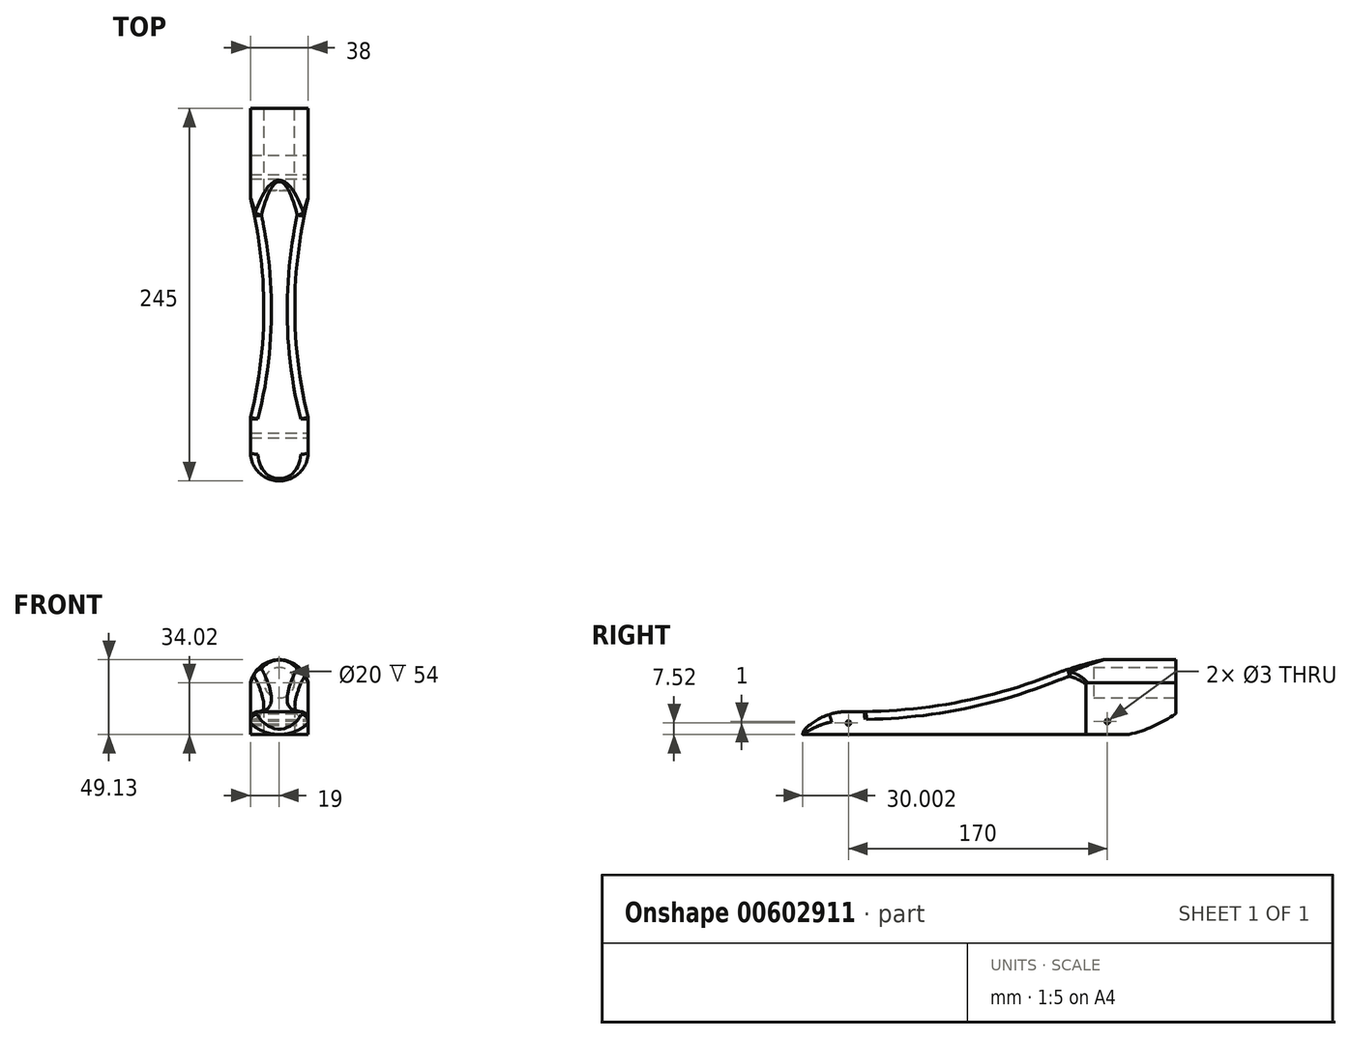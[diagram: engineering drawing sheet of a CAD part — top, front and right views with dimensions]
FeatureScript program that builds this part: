
annotation { "Feature Type Name" : "Feature", "Feature Type Description" : "" }
export const myFeature = defineFeature(function(context is Context, id is Id, definition is map)
    precondition{}
    {
        {
            var Q0;
            Q0=qCreatedBy(makeId("Right.planeOp"),FACE);
            var sketch = newSketch(context, id + "F0", { "sketchPlane" : qUnion([Q0])});
            skLineSegment(sketch, "E0", {"start": v(-162.96, -20) * mm, "end": v(137.04, -20) * mm});
            skLineSegment(sketch, "E1", {"start": v(137.04, -20) * mm, "end": v(137.04, 50) * mm});
            skLineSegment(sketch, "E2", {"start": v(137.04, 50) * mm, "end": v(-162.96, 0) * mm});
            skLineSegment(sketch, "E3", {"start": v(-162.96, 0) * mm, "end": v(-162.96, -20) * mm});
            skSolve(sketch);
        }
        {
            var Q0;
            Q0=makeQuery(id+"F0.imprint","IMPRINT",FACE,{"disambiguationData":[TD([[makeQuery(id+"F0.imprint","IMPRINT",EDGE,{"derivedFrom":sQuery(id+"F0.wireOp",EDGE,"E0")}),1.0]])]});
            extrude(context, id + "F1", {"entities" : qUnion([Q0]), "depth" : 42 * mm, "offsetDistance" : 25 * mm});
        }
        {
            var Q0;
            Q0=makeQuery(id+"F1.opExtrude","SWEPT_FACE",FACE,{"disambiguationData":[OSD([sQuery(id+"F0.wireOp",EDGE,"E1")])]});
            var sketch = newSketch(context, id + "F2", { "sketchPlane" : qUnion([Q0])});
            skCircle(sketch, "E4", {"center": v(-21, 14) * mm, "radius": 10 * mm});
            skSolve(sketch);
        }
        {
            var Q0;
            Q0=makeQuery(id+"F2.imprint","IMPRINT",FACE,{"disambiguationData":[TD([[makeQuery(id+"F2.imprint","IMPRINT",EDGE,{"derivedFrom":sQuery(id+"F2.wireOp",EDGE,"E4")}),1.0]])]});
            extrude(context, id + "F3", {"entities" : qUnion([Q0]), "operationType" : NewBodyOperationType.REMOVE, "oppositeDirection" : true, "depth" : 54 * mm, "offsetDistance" : 25 * mm});
        }
        {
            var Q0;
            Q0=makeQuery(id+"F1.opExtrude","CAP_FACE",FACE,{"disambiguationData":[OSD([sQuery(id+"F0.wireOp",EDGE,"E0"),sQuery(id+"F0.wireOp",EDGE,"E1"),sQuery(id+"F0.wireOp",EDGE,"E2"),sQuery(id+"F0.wireOp",EDGE,"E3")])],"isStart":false});
            var sketch = newSketch(context, id + "F4", { "sketchPlane" : qUnion([Q0])});
            skLineSegment(sketch, "E5", {"start": v(-107.96, -20) * mm, "end": v(-107.96, -18) * mm});
            skArc(sketch, "E6", {"start": v(-77.8, -5) * mm, "mid": v(-10.9, 0.35) * mm, "end": v(53.75, 18.37) * mm});
            skArc(sketch, "E7", {"start": v(137.04, 35) * mm, "mid": v(94.68, 30.25) * mm, "end": v(53.75, 18.37) * mm});
            skArc(sketch, "E8", {"start": v(-77.8, -5) * mm, "mid": v(-94.27, -8.26) * mm, "end": v(-107.96, -18) * mm});
            skArc(sketch, "E9", {"start": v(106.2, -20) * mm, "mid": v(122.27, -14.6) * mm, "end": v(137.04, -6.3) * mm});
            skCircle(sketch, "E10", {"center": v(92.04, -11.5) * mm, "radius": 1.5 * mm});
            skCircle(sketch, "E11", {"center": v(-77.96, -12.5) * mm, "radius": 1.5 * mm});
            skLineSegment(sketch, "E12", {"start": v(-107.96, -20) * mm, "end": v(106.2, -20) * mm});
            skSolve(sketch);
        }
        {
            var Q0;
            {var subQ3=sQuery(id+"F4.wireOp",EDGE,"E5");Q0=makeQuery(id+"F4.imprint","IMPRINT",FACE,{"disambiguationData":[TD([[makeQuery(id+"F4.imprint","IMPRINT",EDGE,{"derivedFrom":subQ3}),1.0]])]});}
            var Q1;
            Q1=makeQuery(id+"F4.imprint","IMPRINT",FACE,{"disambiguationData":[TD([[makeQuery(id+"F4.imprint","IMPRINT",EDGE,{"derivedFrom":sQuery(id+"F4.wireOp",EDGE,"E11")}),1.0]])]});
            var Q2;
            {var subQ0=sQuery(id+"F4.wireOp",EDGE,"E9");Q2=makeQuery(id+"F4.imprint","IMPRINT",FACE,{"disambiguationData":[TD([[makeQuery(id+"F4.imprint","IMPRINT",EDGE,{"derivedFrom":subQ0}),-1.0]])]});}
            var Q3;
            Q3=makeQuery(id+"F4.imprint","IMPRINT",FACE,{"disambiguationData":[TD([[makeQuery(id+"F4.imprint","IMPRINT",EDGE,{"derivedFrom":sQuery(id+"F4.wireOp",EDGE,"E10")}),1.0]])]});
            extrude(context, id + "F5", {"entities" : qUnion([Q0, Q1, Q2, Q3]), "operationType" : NewBodyOperationType.REMOVE, "oppositeDirection" : true, "depth" : 100 * mm, "offsetDistance" : 25 * mm});
        }
        {
            var Q0;
            Q0=makeQuery(id+"F1.opExtrude","SWEPT_FACE",FACE,{"disambiguationData":[OSD([sQuery(id+"F0.wireOp",EDGE,"E0")])]});
            var sketch = newSketch(context, id + "F6", { "sketchPlane" : qUnion([Q0])});
            skLineSegment(sketch, "E13.bottom", {"start": v(2, 111.66) * mm, "end": v(-16.59, 111.66) * mm});
            skLineSegment(sketch, "E13.top", {"start": v(2, -139.51) * mm, "end": v(-16.59, -139.51) * mm});
            skLineSegment(sketch, "E13.left", {"start": v(2, 111.66) * mm, "end": v(2, -139.51) * mm});
            skLineSegment(sketch, "E13.right", {"start": v(-16.59, 111.66) * mm, "end": v(-16.59, -139.51) * mm});
            skPoint(sketch, "E14.firstSnap0", {"position": v(-7.3, 111.66) * mm});
            skLineSegment(sketch, "E14.bottom", {"start": v(40, 111.66) * mm, "end": v(60.24, 111.66) * mm});
            skLineSegment(sketch, "E14.top", {"start": v(40, -140.75) * mm, "end": v(60.24, -140.75) * mm});
            skLineSegment(sketch, "E14.left", {"start": v(40, 111.66) * mm, "end": v(40, -140.75) * mm});
            skLineSegment(sketch, "E14.right", {"start": v(60.24, 111.66) * mm, "end": v(60.24, -140.75) * mm});
            skLineSegment(sketch, "E15", {"start": v(2, 88.96) * mm, "end": v(40, 88.96) * mm});
            skArc(sketch, "E16", {"start": v(40, 88.96) * mm, "mid": v(21, 107.96) * mm, "end": v(2, 88.96) * mm});
            skSolve(sketch);
        }
        {
            var Q0;
            {var subQ0=sQuery(id+"F0.wireOp",EDGE,"E0");var subQ1=makeQuery(id+"F1.opExtrude","CAP_EDGE",EDGE,{"disambiguationData":[OSD([subQ0])],"isStart":true});Q0=makeQuery(id+"F6.imprint","IMPRINT",FACE,{"disambiguationData":[TD([[makeQuery(id+"F6.imprint","IMPRINT",EDGE,{"derivedFrom":subQ1}),1.0]])]});}
            var Q1;
            {var subQ0=sQuery(id+"F0.wireOp",EDGE,"E0");var subQ1=makeQuery(id+"F1.opExtrude","CAP_EDGE",EDGE,{"disambiguationData":[OSD([subQ0])],"isStart":false});Q1=makeQuery(id+"F6.imprint","IMPRINT",FACE,{"disambiguationData":[TD([[makeQuery(id+"F6.imprint","IMPRINT",EDGE,{"derivedFrom":subQ1}),-1.0]])]});}
            var Q2;
            {var subQ1=sQuery(id+"F6.wireOp",EDGE,"E14.bottom");Q2=makeQuery(id+"F6.imprint","IMPRINT",FACE,{"disambiguationData":[TD([[makeQuery(id+"F6.imprint","IMPRINT",EDGE,{"derivedFrom":subQ1}),-1.0]])]});}
            var Q3;
            {var subQ1=sQuery(id+"F6.wireOp",EDGE,"E13.bottom");Q3=makeQuery(id+"F6.imprint","IMPRINT",FACE,{"disambiguationData":[TD([[makeQuery(id+"F6.imprint","IMPRINT",EDGE,{"derivedFrom":subQ1}),1.0]])]});}
            var Q4;
            {var subQ0=sQuery(id+"F6.wireOp",EDGE,"E16");var subQ1=sQuery(id+"F6.wireOp",EDGE,"E13.left");var subQ2=makeQuery(id+"F6.imprint","INTERSECT",VERTEX,{"derivedFrom":[subQ1,sQuery(id+"F6.wireOp",EDGE,"E15"),subQ0]});Q4=makeQuery(id+"F6.imprint","IMPRINT",FACE,{"disambiguationData":[TD([[makeQuery(id+"F6.imprint","IMPRINT",EDGE,{"disambiguationData":[TD([[subQ2,1.0]])],"derivedFrom":subQ1}),1.0]])]});}
            var Q5;
            {var subQ0=sQuery(id+"F6.wireOp",EDGE,"E16");var subQ1=sQuery(id+"F6.wireOp",EDGE,"E14.left");var subQ2=makeQuery(id+"F6.imprint","INTERSECT",VERTEX,{"derivedFrom":[subQ1,sQuery(id+"F6.wireOp",EDGE,"E15"),subQ0]});Q5=makeQuery(id+"F6.imprint","IMPRINT",FACE,{"disambiguationData":[TD([[makeQuery(id+"F6.imprint","IMPRINT",EDGE,{"disambiguationData":[TD([[subQ2,1.0]])],"derivedFrom":subQ1}),-1.0]])]});}
            extrude(context, id + "F7", {"entities" : qUnion([Q0, Q1, Q2, Q3, Q4, Q5]), "operationType" : NewBodyOperationType.REMOVE, "oppositeDirection" : true, "depth" : 100 * mm, "offsetDistance" : 25 * mm});
        }
        {
            var Q0;
            Q0=makeQuery(id+"F1.opExtrude","SWEPT_FACE",FACE,{"disambiguationData":[OSD([sQuery(id+"F0.wireOp",EDGE,"E1")])]});
            var sketch = newSketch(context, id + "F8", { "sketchPlane" : qUnion([Q0])});
            skLineSegment(sketch, "E17", {"start": v(-40, 14) * mm, "end": v(-2, 14) * mm});
            skArc(sketch, "E18", {"start": v(-2, 14) * mm, "mid": v(-21, 29.11) * mm, "end": v(-40, 14) * mm});
            skSolve(sketch);
        }
        {
            var Q0;
            {var subQ0=sQuery(id+"F8.wireOp",EDGE,"E18");Q0=makeQuery(id+"F8.imprint","IMPRINT",FACE,{"disambiguationData":[TD([[makeQuery(id+"F8.imprint","IMPRINT",EDGE,{"derivedFrom":subQ0}),-1.0]])]});}
            extrude(context, id + "F9", {"entities" : qUnion([Q0]), "operationType" : NewBodyOperationType.REMOVE, "oppositeDirection" : true, "depth" : 300 * mm, "offsetDistance" : 25 * mm});
        }
        {
            var Q0;
            Q0=makeQuery(id+"F1.opExtrude","SWEPT_FACE",FACE,{"disambiguationData":[OSD([sQuery(id+"F0.wireOp",EDGE,"E0")])]});
            var sketch = newSketch(context, id + "F10", { "sketchPlane" : qUnion([Q0])});
            skArc(sketch, "E19", {"start": v(40, 66.64) * mm, "mid": v(31.16, -5.63) * mm, "end": v(40, -77.9) * mm});
            skArc(sketch, "E20", {"start": v(2, -77.9) * mm, "mid": v(10.84, -5.63) * mm, "end": v(2, 66.64) * mm});
            skLineSegment(sketch, "E21", {"start": v(40, 66.64) * mm, "end": v(40, -77.9) * mm});
            skLineSegment(sketch, "E22", {"start": v(2, 66.64) * mm, "end": v(2, -77.9) * mm});
            skSolve(sketch);
        }
        {
            var Q0;
            Q0=makeQuery(id+"F10.imprint","IMPRINT",FACE,{"disambiguationData":[TD([[makeQuery(id+"F10.imprint","IMPRINT",EDGE,{"derivedFrom":sQuery(id+"F10.wireOp",EDGE,"E20")}),1.0]])]});
            var Q1;
            Q1=makeQuery(id+"F10.imprint","IMPRINT",FACE,{"disambiguationData":[TD([[makeQuery(id+"F10.imprint","IMPRINT",EDGE,{"derivedFrom":sQuery(id+"F10.wireOp",EDGE,"E19")}),1.0]])]});
            extrude(context, id + "F11", {"entities" : qUnion([Q0, Q1]), "operationType" : NewBodyOperationType.REMOVE, "oppositeDirection" : true, "depth" : 100 * mm, "offsetDistance" : 25 * mm});
        }
        {
            var Q0;
            Q0=makeQuery(id+"F9.boolean.opBoolean","INTERSECT",EDGE,{"derivedFrom":[makeQuery(id+"F5.boolean.opBoolean","COPY",FACE,{"derivedFrom":makeQuery(id+"F5.opExtrude","SWEPT_FACE",FACE,{"disambiguationData":[OSD([sQuery(id+"F4.wireOp",EDGE,"E7")])]})}),makeQuery(id+"F9.opExtrude","SWEPT_FACE",FACE,{"disambiguationData":[OSD([sQuery(id+"F8.wireOp",EDGE,"E18")])]})]});
            var Q1;
            Q1=makeQuery(id+"F11.boolean.opBoolean","INTERSECT",EDGE,{"derivedFrom":[makeQuery(id+"F5.boolean.opBoolean","COPY",FACE,{"derivedFrom":makeQuery(id+"F5.opExtrude","SWEPT_FACE",FACE,{"disambiguationData":[OSD([sQuery(id+"F4.wireOp",EDGE,"E6")])]})}),makeQuery(id+"F11.opExtrude","SWEPT_FACE",FACE,{"disambiguationData":[OSD([sQuery(id+"F10.wireOp",EDGE,"E19")])]})]});
            var Q2;
            Q2=makeQuery(id+"F5.boolean.opBoolean","COPY",EDGE,{"derivedFrom":makeQuery(id+"F5.opExtrude","SWEPT_EDGE",EDGE,{"disambiguationData":[OSD([sQuery(id+"F4.wireOp",EDGE,"E6"),sQuery(id+"F4.wireOp",EDGE,"E7")])]})});
            var Q3;
            Q3=makeQuery(id+"F11.boolean.opBoolean","INTERSECT",EDGE,{"derivedFrom":[makeQuery(id+"F5.boolean.opBoolean","COPY",FACE,{"derivedFrom":makeQuery(id+"F5.opExtrude","SWEPT_FACE",FACE,{"disambiguationData":[OSD([sQuery(id+"F4.wireOp",EDGE,"E6")])]})}),makeQuery(id+"F11.opExtrude","SWEPT_FACE",FACE,{"disambiguationData":[OSD([sQuery(id+"F10.wireOp",EDGE,"E20")])]})]});
            var Q4;
            {var subQ0=sQuery(id+"F6.wireOp",EDGE,"E13.left");Q4=makeQuery(id+"F7.boolean.opBoolean","INTERSECT",EDGE,{"derivedFrom":[makeQuery(id+"F5.boolean.opBoolean","COPY",FACE,{"derivedFrom":makeQuery(id+"F5.opExtrude","SWEPT_FACE",FACE,{"disambiguationData":[OSD([sQuery(id+"F4.wireOp",EDGE,"E8")])]})}),makeQuery(id+"F7.opExtrude","SWEPT_FACE",FACE,{"disambiguationData":[OSD([subQ0]),TDD([makeQuery(id+"F6.imprint","IMPRINT",EDGE,{"disambiguationData":[TD([[makeQuery(id+"F6.imprint","INTERSECT",VERTEX,{"derivedFrom":[subQ0,sQuery(id+"F6.wireOp",EDGE,"E15"),sQuery(id+"F6.wireOp",EDGE,"E16")]}),-1.0]])],"derivedFrom":subQ0}),makeQuery(id+"F6.imprint","IMPRINT",EDGE,{"disambiguationData":[TD([[makeQuery(id+"F6.imprint","INTERSECT",VERTEX,{"derivedFrom":[sQuery(id+"F6.wireOp",EDGE,"E13.top"),subQ0]}),1.0]])],"derivedFrom":subQ0})])]})]});}
            var Q5;
            {var subQ0=sQuery(id+"F6.wireOp",EDGE,"E14.left");Q5=makeQuery(id+"F7.boolean.opBoolean","INTERSECT",EDGE,{"derivedFrom":[makeQuery(id+"F5.boolean.opBoolean","COPY",FACE,{"derivedFrom":makeQuery(id+"F5.opExtrude","SWEPT_FACE",FACE,{"disambiguationData":[OSD([sQuery(id+"F4.wireOp",EDGE,"E8")])]})}),makeQuery(id+"F7.opExtrude","SWEPT_FACE",FACE,{"disambiguationData":[OSD([subQ0]),TDD([makeQuery(id+"F6.imprint","IMPRINT",EDGE,{"disambiguationData":[TD([[makeQuery(id+"F6.imprint","INTERSECT",VERTEX,{"derivedFrom":[subQ0,sQuery(id+"F6.wireOp",EDGE,"E15"),sQuery(id+"F6.wireOp",EDGE,"E16")]}),-1.0]])],"derivedFrom":subQ0}),makeQuery(id+"F6.imprint","IMPRINT",EDGE,{"disambiguationData":[TD([[makeQuery(id+"F6.imprint","INTERSECT",VERTEX,{"derivedFrom":[sQuery(id+"F6.wireOp",EDGE,"E14.top"),subQ0]}),1.0]])],"derivedFrom":subQ0})])]})]});}
            var Q6;
            Q6=makeQuery(id+"F9.boolean.opBoolean","COPY",EDGE,{"derivedFrom":makeQuery(id+"F9.opExtrude","SWEPT_EDGE",EDGE,{"disambiguationData":[OSD([sQuery(id+"F0.wireOp",EDGE,"E1"),sQuery(id+"F6.wireOp",EDGE,"E14.left"),sQuery(id+"F8.wireOp",EDGE,"E17"),sQuery(id+"F8.wireOp",EDGE,"E18")])]})});
            var Q7;
            {var subQ0=sQuery(id+"F10.wireOp",EDGE,"E21");var subQ1=sQuery(id+"F10.wireOp",EDGE,"E19");var subQ2=sQuery(id+"F6.wireOp",EDGE,"E14.left");Q7=makeQuery(id+"F11.boolean.opBoolean","COPY",EDGE,{"derivedFrom":makeQuery(id+"F11.opExtrude","SWEPT_EDGE",EDGE,{"disambiguationData":[OSD([subQ2,subQ1,subQ0]),TDD([makeQuery(id+"F10.imprint","INTERSECT",VERTEX,{"disambiguationData":[OD(1.0)],"derivedFrom":[makeQuery(id+"F7.boolean.opBoolean","COPY",EDGE,{"derivedFrom":makeQuery(id+"F7.opExtrude","CAP_EDGE",EDGE,{"disambiguationData":[OSD([subQ2]),TDD([makeQuery(id+"F6.imprint","IMPRINT",EDGE,{"disambiguationData":[TD([[makeQuery(id+"F6.imprint","INTERSECT",VERTEX,{"derivedFrom":[subQ2,sQuery(id+"F6.wireOp",EDGE,"E15"),sQuery(id+"F6.wireOp",EDGE,"E16")]}),-1.0]])],"derivedFrom":subQ2}),makeQuery(id+"F6.imprint","IMPRINT",EDGE,{"disambiguationData":[TD([[makeQuery(id+"F6.imprint","INTERSECT",VERTEX,{"derivedFrom":[sQuery(id+"F6.wireOp",EDGE,"E14.top"),subQ2]}),1.0]])],"derivedFrom":subQ2})])],"isStart":true})}),subQ1,subQ0]})])]})});}
            var Q8;
            Q8=makeQuery(id+"F11.boolean.opBoolean","INTERSECT",EDGE,{"derivedFrom":[makeQuery(id+"F9.boolean.opBoolean","COPY",FACE,{"derivedFrom":makeQuery(id+"F9.opExtrude","SWEPT_FACE",FACE,{"disambiguationData":[OSD([sQuery(id+"F8.wireOp",EDGE,"E18")])]})}),makeQuery(id+"F11.opExtrude","SWEPT_FACE",FACE,{"disambiguationData":[OSD([sQuery(id+"F10.wireOp",EDGE,"E19")])]})]});
            var Q9;
            Q9=makeQuery(id+"F11.boolean.opBoolean","INTERSECT",EDGE,{"derivedFrom":[makeQuery(id+"F9.boolean.opBoolean","COPY",FACE,{"derivedFrom":makeQuery(id+"F9.opExtrude","SWEPT_FACE",FACE,{"disambiguationData":[OSD([sQuery(id+"F8.wireOp",EDGE,"E18")])]})}),makeQuery(id+"F11.opExtrude","SWEPT_FACE",FACE,{"disambiguationData":[OSD([sQuery(id+"F10.wireOp",EDGE,"E20")])]})]});
            var Q10;
            {var subQ0=sQuery(id+"F10.wireOp",EDGE,"E22");var subQ1=sQuery(id+"F10.wireOp",EDGE,"E20");var subQ2=sQuery(id+"F6.wireOp",EDGE,"E13.left");Q10=makeQuery(id+"F11.boolean.opBoolean","COPY",EDGE,{"derivedFrom":makeQuery(id+"F11.opExtrude","SWEPT_EDGE",EDGE,{"disambiguationData":[OSD([subQ2,subQ1,subQ0]),TDD([makeQuery(id+"F10.imprint","INTERSECT",VERTEX,{"disambiguationData":[OD(0.0)],"derivedFrom":[makeQuery(id+"F7.boolean.opBoolean","COPY",EDGE,{"derivedFrom":makeQuery(id+"F7.opExtrude","CAP_EDGE",EDGE,{"disambiguationData":[OSD([subQ2]),TDD([makeQuery(id+"F6.imprint","IMPRINT",EDGE,{"disambiguationData":[TD([[makeQuery(id+"F6.imprint","INTERSECT",VERTEX,{"derivedFrom":[subQ2,sQuery(id+"F6.wireOp",EDGE,"E15"),sQuery(id+"F6.wireOp",EDGE,"E16")]}),-1.0]])],"derivedFrom":subQ2}),makeQuery(id+"F6.imprint","IMPRINT",EDGE,{"disambiguationData":[TD([[makeQuery(id+"F6.imprint","INTERSECT",VERTEX,{"derivedFrom":[sQuery(id+"F6.wireOp",EDGE,"E13.top"),subQ2]}),1.0]])],"derivedFrom":subQ2})])],"isStart":true})}),subQ1,subQ0]})])]})});}
            var Q11;
            Q11=makeQuery(id+"F9.boolean.opBoolean","COPY",EDGE,{"derivedFrom":makeQuery(id+"F9.opExtrude","SWEPT_EDGE",EDGE,{"disambiguationData":[OSD([sQuery(id+"F0.wireOp",EDGE,"E1"),sQuery(id+"F6.wireOp",EDGE,"E13.left"),sQuery(id+"F8.wireOp",EDGE,"E17"),sQuery(id+"F8.wireOp",EDGE,"E18")])]})});
            var Q12;
            Q12=makeQuery(id+"F5.boolean.opBoolean","COPY",EDGE,{"derivedFrom":makeQuery(id+"F5.opExtrude","SWEPT_EDGE",EDGE,{"disambiguationData":[OSD([sQuery(id+"F0.wireOp",EDGE,"E0"),sQuery(id+"F4.wireOp",EDGE,"E9"),sQuery(id+"F4.wireOp",EDGE,"E12")])]})});
            fillet(context, id + "F12", {"entities" : qUnion([Q0, Q1, Q2, Q3, Q4, Q5, Q6, Q7, Q8, Q9, Q10, Q11, Q12]), "radius" : 5 * mm, "tangentPropagation" : true, "allowEdgeOverflow" : false});
        }
        {
            var Q0;
            {var subQ0=sQuery(id+"F10.wireOp",EDGE,"E21");var subQ1=sQuery(id+"F10.wireOp",EDGE,"E19");var subQ2=sQuery(id+"F6.wireOp",EDGE,"E14.left");Q0=makeQuery(id+"F11.boolean.opBoolean","COPY",EDGE,{"derivedFrom":makeQuery(id+"F11.opExtrude","SWEPT_EDGE",EDGE,{"disambiguationData":[OSD([subQ2,subQ1,subQ0]),TDD([makeQuery(id+"F10.imprint","INTERSECT",VERTEX,{"disambiguationData":[OD(0.0)],"derivedFrom":[makeQuery(id+"F7.boolean.opBoolean","COPY",EDGE,{"derivedFrom":makeQuery(id+"F7.opExtrude","CAP_EDGE",EDGE,{"disambiguationData":[OSD([subQ2]),TDD([makeQuery(id+"F6.imprint","IMPRINT",EDGE,{"disambiguationData":[TD([[makeQuery(id+"F6.imprint","INTERSECT",VERTEX,{"derivedFrom":[subQ2,sQuery(id+"F6.wireOp",EDGE,"E15"),sQuery(id+"F6.wireOp",EDGE,"E16")]}),-1.0]])],"derivedFrom":subQ2}),makeQuery(id+"F6.imprint","IMPRINT",EDGE,{"disambiguationData":[TD([[makeQuery(id+"F6.imprint","INTERSECT",VERTEX,{"derivedFrom":[sQuery(id+"F6.wireOp",EDGE,"E14.top"),subQ2]}),1.0]])],"derivedFrom":subQ2})])],"isStart":true})}),subQ1,subQ0]})])]})});}
            var Q1;
            Q1=makeQuery(id+"F7.boolean.opBoolean","COPY",EDGE,{"derivedFrom":makeQuery(id+"F7.opExtrude","SWEPT_EDGE",EDGE,{"disambiguationData":[OSD([sQuery(id+"F6.wireOp",EDGE,"E14.left"),sQuery(id+"F6.wireOp",EDGE,"E15"),sQuery(id+"F6.wireOp",EDGE,"E16")])]})});
            var Q2;
            {var subQ0=sQuery(id+"F10.wireOp",EDGE,"E22");var subQ1=sQuery(id+"F10.wireOp",EDGE,"E20");var subQ2=sQuery(id+"F6.wireOp",EDGE,"E13.left");Q2=makeQuery(id+"F11.boolean.opBoolean","COPY",EDGE,{"derivedFrom":makeQuery(id+"F11.opExtrude","SWEPT_EDGE",EDGE,{"disambiguationData":[OSD([subQ2,subQ1,subQ0]),TDD([makeQuery(id+"F10.imprint","INTERSECT",VERTEX,{"disambiguationData":[OD(1.0)],"derivedFrom":[makeQuery(id+"F7.boolean.opBoolean","COPY",EDGE,{"derivedFrom":makeQuery(id+"F7.opExtrude","CAP_EDGE",EDGE,{"disambiguationData":[OSD([subQ2]),TDD([makeQuery(id+"F6.imprint","IMPRINT",EDGE,{"disambiguationData":[TD([[makeQuery(id+"F6.imprint","INTERSECT",VERTEX,{"derivedFrom":[subQ2,sQuery(id+"F6.wireOp",EDGE,"E15"),sQuery(id+"F6.wireOp",EDGE,"E16")]}),-1.0]])],"derivedFrom":subQ2}),makeQuery(id+"F6.imprint","IMPRINT",EDGE,{"disambiguationData":[TD([[makeQuery(id+"F6.imprint","INTERSECT",VERTEX,{"derivedFrom":[sQuery(id+"F6.wireOp",EDGE,"E13.top"),subQ2]}),1.0]])],"derivedFrom":subQ2})])],"isStart":true})}),subQ1,subQ0]})])]})});}
            var Q3;
            Q3=makeQuery(id+"F7.boolean.opBoolean","COPY",EDGE,{"derivedFrom":makeQuery(id+"F7.opExtrude","SWEPT_EDGE",EDGE,{"disambiguationData":[OSD([sQuery(id+"F6.wireOp",EDGE,"E13.left"),sQuery(id+"F6.wireOp",EDGE,"E15"),sQuery(id+"F6.wireOp",EDGE,"E16")])]})});
            fillet(context, id + "F13", {"entities" : qUnion([Q0, Q1, Q2, Q3]), "radius" : 5 * mm, "tangentPropagation" : true, "allowEdgeOverflow" : false});
        }
    });
